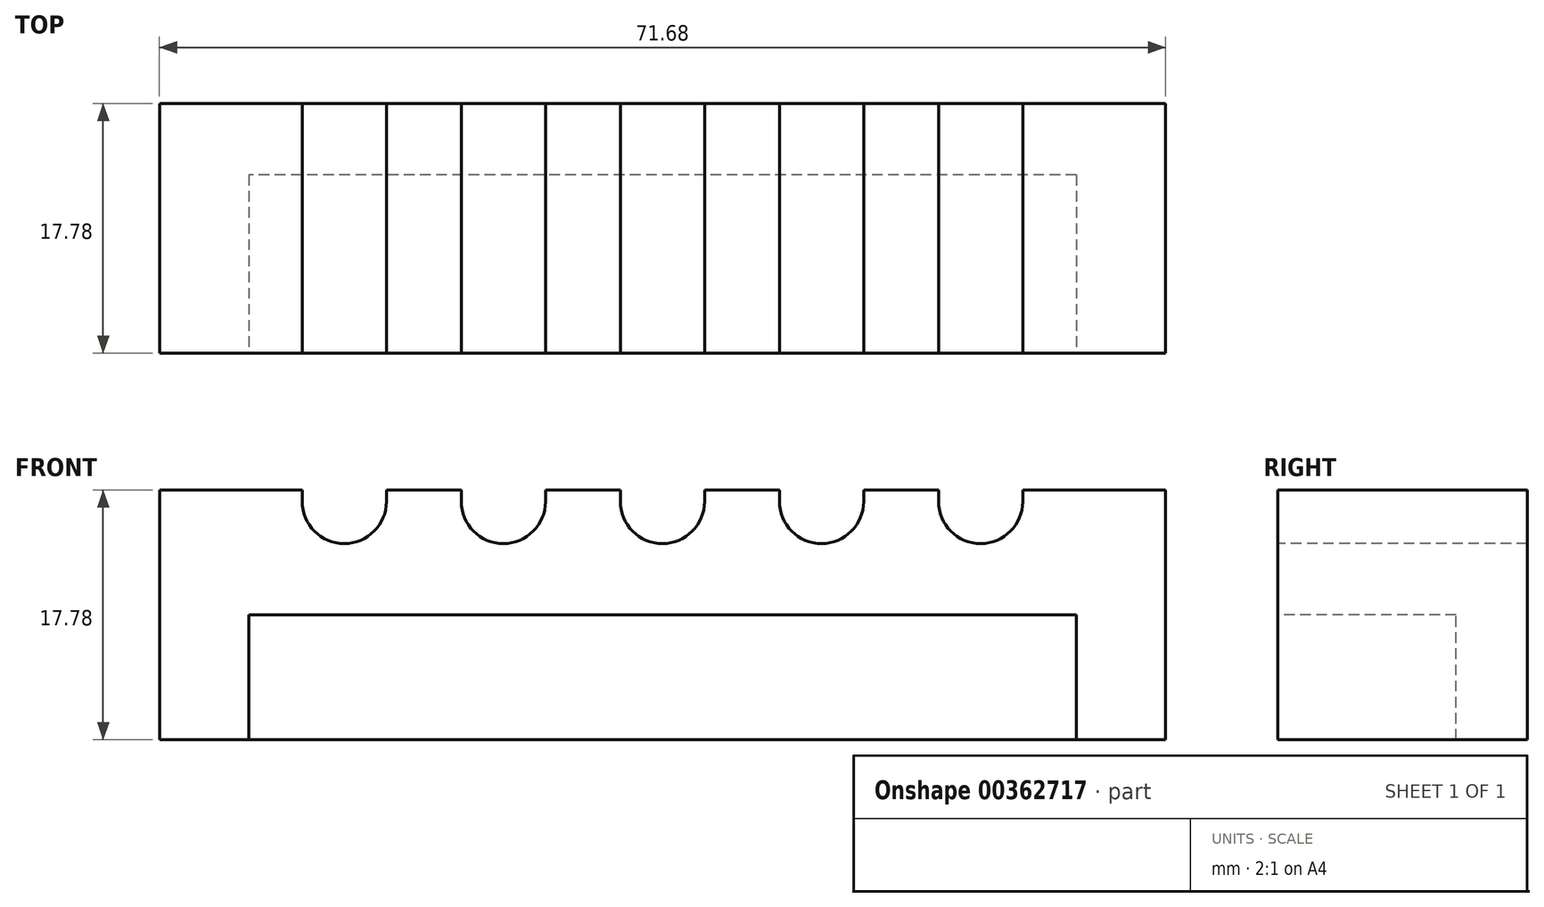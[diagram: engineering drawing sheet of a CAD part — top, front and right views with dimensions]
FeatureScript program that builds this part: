
annotation { "Feature Type Name" : "Feature", "Feature Type Description" : "" }
export const myFeature = defineFeature(function(context is Context, id is Id, definition is map)
    precondition{}
    {
        {
            var Q0;
            Q0=qCreatedBy(makeId("Front.planeOp"),FACE);
            var sketch = newSketch(context, id + "F0", { "sketchPlane" : qUnion([Q0])});
            skLineSegment(sketch, "E0.bottom", {"start": v(35.84, -8.89) * mm, "end": v(-35.84, -8.89) * mm});
            skLineSegment(sketch, "E0.top", {"start": v(35.84, 8.9) * mm, "end": v(-35.84, 8.89) * mm});
            skLineSegment(sketch, "E0.left", {"start": v(35.84, -8.89) * mm, "end": v(35.84, 8.9) * mm});
            skLineSegment(sketch, "E0.right", {"start": v(-35.84, -8.89) * mm, "end": v(-35.84, 8.9) * mm});
            skPoint(sketch, "E0.middle", {"position": v(0, 0) * mm});
            skSolve(sketch);
        }
        {
            var Q0;
            Q0=qSketchRegion(id+"F0",true);
            extrude(context, id + "F1", {"entities" : qUnion([Q0]), "endBound" : BoundingType.SYMMETRIC, "depth" : 17.78 * mm});
        }
        {
            var Q0;
            Q0=makeQuery(id+"F1.opExtrude","CAP_FACE",FACE,{"disambiguationData":[OSD([sQuery(id+"F0.wireOp",EDGE,"E0.bottom"),sQuery(id+"F0.wireOp",EDGE,"E0.top"),sQuery(id+"F0.wireOp",EDGE,"E0.left"),sQuery(id+"F0.wireOp",EDGE,"E0.right")])],"isStart":false});
            var sketch = newSketch(context, id + "F2", { "sketchPlane" : qUnion([Q0])});
            skLineSegment(sketch, "E1.bottom", {"start": v(-25.67, 8.89) * mm, "end": v(-19.67, 8.89) * mm});
            skLineSegment(sketch, "E1.left", {"start": v(-25.67, 8.9) * mm, "end": v(-25.67, 8.08) * mm});
            skLineSegment(sketch, "E1.right", {"start": v(-19.67, 8.9) * mm, "end": v(-19.67, 8.08) * mm});
            skLineSegment(sketch, "E2.direction1", {"start": v(-25.67, 8.08) * mm, "end": v(-19.67, 8.08) * mm, "construction": true});
            skArc(sketch, "E3", {"start": v(-25.67, 8.08) * mm, "mid": v(-22.67, 5.08) * mm, "end": v(-19.67, 8.08) * mm});
            skLineSegment(sketch, "E4.trimOffspring", {"start": v(-25.67, 8.08) * mm, "end": v(-19.67, 8.08) * mm});
            skLineSegment(sketch, "E5.1.0.0", {"start": v(-8.33, 8.9) * mm, "end": v(-8.33, 8.08) * mm});
            skLineSegment(sketch, "E5.1.0.1", {"start": v(-14.33, 8.89) * mm, "end": v(-8.33, 8.89) * mm});
            skLineSegment(sketch, "E5.1.0.2", {"start": v(-14.33, 8.9) * mm, "end": v(-14.33, 8.08) * mm});
            skArc(sketch, "E5.1.0.3", {"start": v(-14.33, 8.08) * mm, "mid": v(-11.33, 5.08) * mm, "end": v(-8.33, 8.08) * mm});
            skLineSegment(sketch, "E5.1.0.4", {"start": v(-14.33, 8.08) * mm, "end": v(-8.33, 8.08) * mm, "construction": true});
            skArc(sketch, "E5.1.0.5", {"start": v(-14.33, 8.08) * mm, "mid": v(-11.33, 5.08) * mm, "end": v(-8.33, 8.08) * mm});
            skLineSegment(sketch, "E5.2.0.0", {"start": v(3, 8.9) * mm, "end": v(3, 8.08) * mm});
            skLineSegment(sketch, "E5.2.0.1", {"start": v(-3, 8.89) * mm, "end": v(3, 8.89) * mm});
            skLineSegment(sketch, "E5.2.0.2", {"start": v(-3, 8.9) * mm, "end": v(-3, 8.08) * mm});
            skArc(sketch, "E5.2.0.3", {"start": v(-3, 8.08) * mm, "mid": v(0, 5.08) * mm, "end": v(3, 8.08) * mm});
            skLineSegment(sketch, "E5.2.0.4", {"start": v(-3, 8.08) * mm, "end": v(3, 8.08) * mm});
            skArc(sketch, "E5.2.0.5", {"start": v(-3, 8.08) * mm, "mid": v(0, 5.08) * mm, "end": v(3, 8.08) * mm});
            skLineSegment(sketch, "E5.3.0.0", {"start": v(14.33, 8.9) * mm, "end": v(14.33, 8.08) * mm});
            skLineSegment(sketch, "E5.3.0.1", {"start": v(8.33, 8.89) * mm, "end": v(14.33, 8.89) * mm});
            skLineSegment(sketch, "E5.3.0.2", {"start": v(8.33, 8.9) * mm, "end": v(8.33, 8.08) * mm});
            skArc(sketch, "E5.3.0.3", {"start": v(8.33, 8.08) * mm, "mid": v(11.33, 5.08) * mm, "end": v(14.33, 8.08) * mm});
            skLineSegment(sketch, "E5.3.0.4", {"start": v(8.33, 8.08) * mm, "end": v(14.33, 8.08) * mm});
            skArc(sketch, "E5.3.0.5", {"start": v(8.33, 8.08) * mm, "mid": v(11.33, 5.08) * mm, "end": v(14.33, 8.08) * mm});
            skLineSegment(sketch, "E5.direction1", {"start": v(-19.67, 8.08) * mm, "end": v(-8.33, 8.08) * mm, "construction": true});
            skLineSegment(sketch, "E6", {"start": v(-14.33, 8.08) * mm, "end": v(-8.33, 8.08) * mm});
            skLineSegment(sketch, "E7", {"start": v(0, 8.89) * mm, "end": v(0, -8.89) * mm, "construction": true});
            skLineSegment(sketch, "E8.0.4.0", {"start": v(25.67, 8.9) * mm, "end": v(25.67, 8.08) * mm});
            skLineSegment(sketch, "E8.3.4.0", {"start": v(19.67, 8.89) * mm, "end": v(25.67, 8.89) * mm});
            skLineSegment(sketch, "E8.6.4.0", {"start": v(19.67, 8.9) * mm, "end": v(19.67, 8.08) * mm});
            skArc(sketch, "E8.9.4.0", {"start": v(19.67, 8.08) * mm, "mid": v(22.67, 5.08) * mm, "end": v(25.67, 8.08) * mm});
            skLineSegment(sketch, "E8.13.4.0", {"start": v(19.67, 8.08) * mm, "end": v(25.67, 8.08) * mm, "construction": true});
            skArc(sketch, "E8.16.4.0", {"start": v(19.67, 8.08) * mm, "mid": v(22.67, 5.08) * mm, "end": v(25.67, 8.08) * mm});
            skPoint(sketch, "E9", {"position": v(-22.67, 5.08) * mm});
            skSolve(sketch);
        }
        {
            var Q0;
            Q0=qSketchRegion(id+"F2",true);
            extrude(context, id + "F3", {"entities" : qUnion([Q0]), "operationType" : NewBodyOperationType.REMOVE, "endBound" : BoundingType.THROUGH_ALL, "oppositeDirection" : true, "depth" : 25.4 * mm});
        }
        {
            var Q0;
            Q0=makeQuery(id+"F1.opExtrude","CAP_FACE",FACE,{"disambiguationData":[OSD([sQuery(id+"F0.wireOp",EDGE,"E0.bottom"),sQuery(id+"F0.wireOp",EDGE,"E0.top"),sQuery(id+"F0.wireOp",EDGE,"E0.left"),sQuery(id+"F0.wireOp",EDGE,"E0.right")])],"isStart":false});
            var sketch = newSketch(context, id + "F4", { "sketchPlane" : qUnion([Q0])});
            skLineSegment(sketch, "E10.bottom", {"start": v(-29.49, -8.89) * mm, "end": v(29.48, -8.89) * mm});
            skLineSegment(sketch, "E10.left", {"start": v(-29.48, -8.89) * mm, "end": v(-29.48, 0) * mm});
            skLineSegment(sketch, "E10.right", {"start": v(29.48, -8.89) * mm, "end": v(29.48, 0) * mm});
            skLineSegment(sketch, "E11", {"start": v(-29.48, 0) * mm, "end": v(29.48, 0) * mm});
            skPoint(sketch, "E12", {"position": v(0, 0) * mm});
            skSolve(sketch);
        }
        {
            var Q0;
            Q0=qSketchRegion(id+"F4",true);
            extrude(context, id + "F5", {"entities" : qUnion([Q0]), "operationType" : NewBodyOperationType.REMOVE, "oppositeDirection" : true, "depth" : 12.7 * mm});
        }
    });
